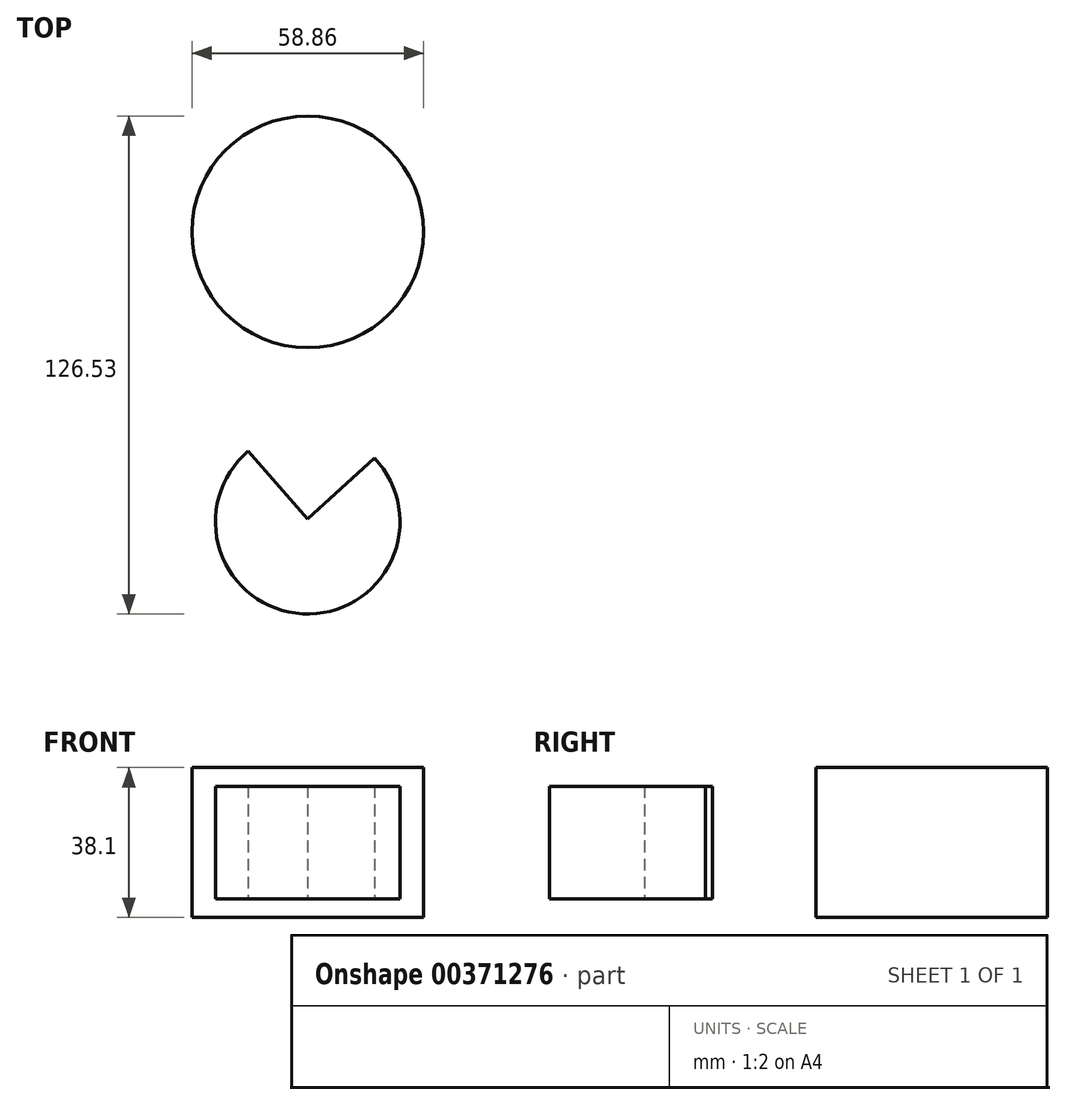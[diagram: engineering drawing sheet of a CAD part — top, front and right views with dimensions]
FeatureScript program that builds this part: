
annotation { "Feature Type Name" : "Feature", "Feature Type Description" : "" }
export const myFeature = defineFeature(function(context is Context, id is Id, definition is map)
    precondition{}
    {
        {
            var Q0;
            Q0=qCreatedBy(makeId("Top.planeOp"),FACE);
            var sketch = newSketch(context, id + "F0", { "sketchPlane" : qUnion([Q0])});
            skCircle(sketch, "E0", {"center": v(0, -26.76) * mm, "radius": 23.44 * mm});
            skCircle(sketch, "E1", {"center": v(0, 46.89) * mm, "radius": 29.43 * mm});
            skSolve(sketch);
        }
        {
            var Q0;
            Q0 = qSketchRegion(id + "F0", true);
            var sketch = newSketch(context, id + "F1", { "sketchPlane" : qUnion([Q0])});
            skLineSegment(sketch, "E2", {"start": v(0, 46.68) * mm, "end": v(28.63, 0) * mm});
            skLineSegment(sketch, "E3", {"start": v(0, 46.68) * mm, "end": v(-22.83, 0) * mm});
            skLineSegment(sketch, "E4", {"start": v(-22.83, 0) * mm, "end": v(0, -26.09) * mm});
            skLineSegment(sketch, "E5", {"start": v(0, -26.09) * mm, "end": v(28.63, 0) * mm});
            skSolve(sketch);
        }
        {
            var Q0;
            {var subQ0=sQuery(id+"F1.wireOp",EDGE,"E5");var subQ1=sQuery(id+"F1.wireOp",EDGE,"E4");var subQ2=makeQuery(id+"F1.imprint","INTERSECT",VERTEX,{"derivedFrom":[subQ1,subQ0]});Q0=makeQuery(id+"F1.imprint","IMPRINT",FACE,{"disambiguationData":[TD([[makeQuery(id+"F1.imprint","IMPRINT",EDGE,{"disambiguationData":[TD([[subQ2,1.0]])],"derivedFrom":subQ1}),-1.0]])]});}
            extrude(context, id + "F2", {"entities" : qUnion([Q0]), "endBound" : BoundingType.SYMMETRIC, "depth" : 28.6 * mm});
        }
        {
            var Q0;
            Q0=makeQuery(id+"F0.imprint","IMPRINT",FACE,{"disambiguationData":[TD([[makeQuery(id+"F0.imprint","IMPRINT",EDGE,{"derivedFrom":sQuery(id+"F0.wireOp",EDGE,"E1")}),1.0]])]});
            extrude(context, id + "F3", {"entities" : qUnion([Q0]), "endBound" : BoundingType.SYMMETRIC, "depth" : 38.1 * mm});
        }
    });
